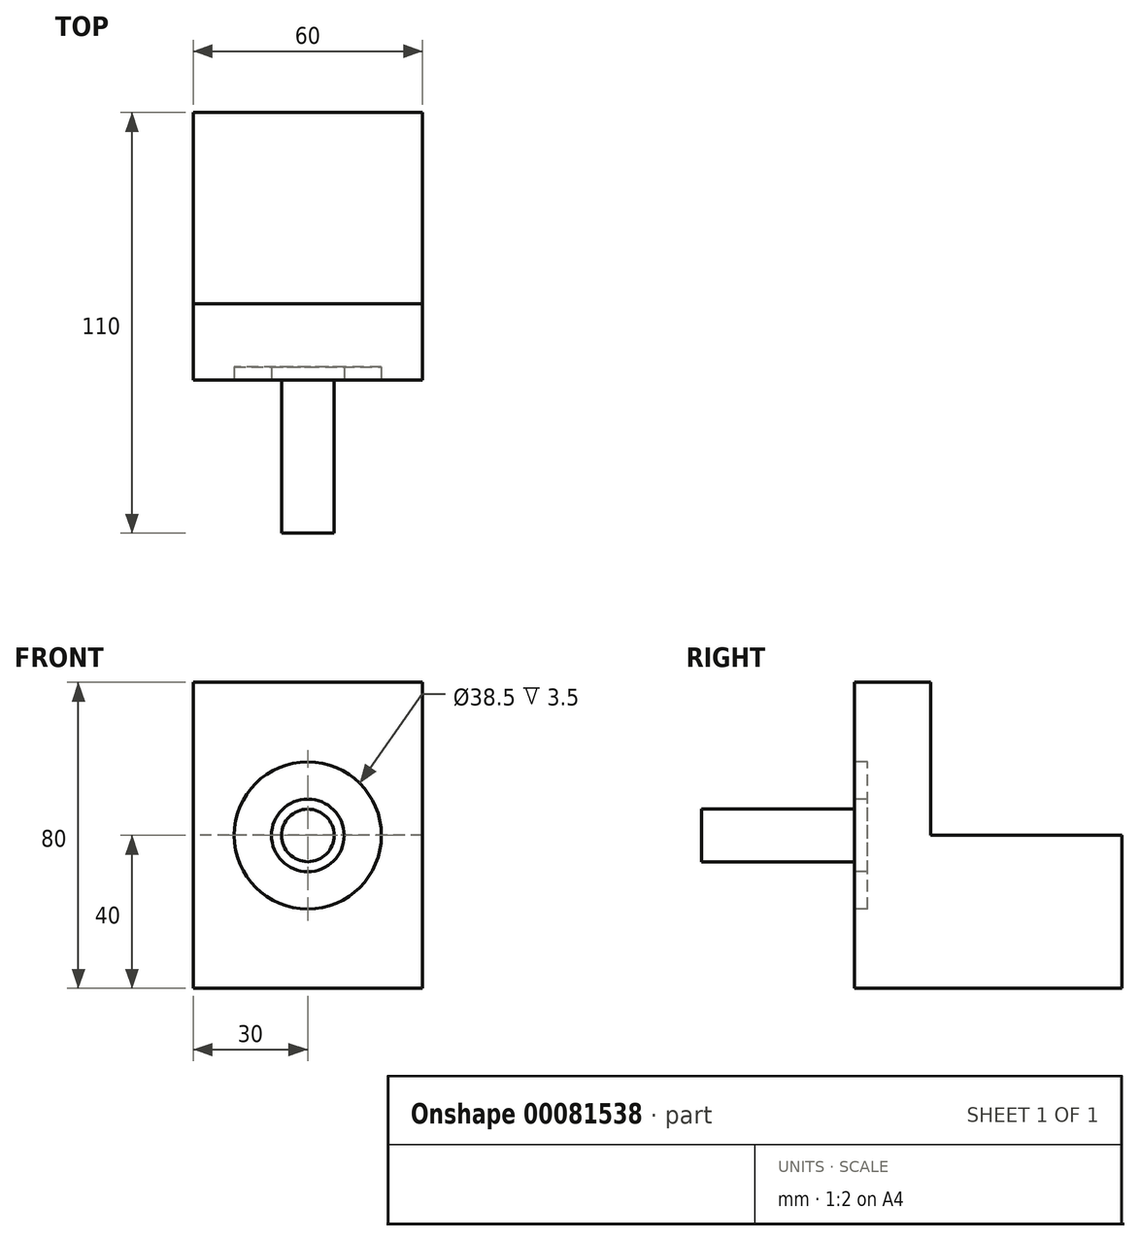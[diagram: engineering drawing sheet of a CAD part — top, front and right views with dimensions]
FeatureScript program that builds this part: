
annotation { "Feature Type Name" : "Feature", "Feature Type Description" : "" }
export const myFeature = defineFeature(function(context is Context, id is Id, definition is map)
    precondition{}
    {
        {
            var Q0;
            Q0=qCreatedBy(makeId("Front.planeOp"),FACE);
            var sketch = newSketch(context, id + "F0", { "sketchPlane" : qUnion([Q0])});
            skLineSegment(sketch, "E0", {"start": v(-30, 0) * mm, "end": v(30, 0) * mm});
            skLineSegment(sketch, "E1", {"start": v(30, 0) * mm, "end": v(30, 80) * mm});
            skLineSegment(sketch, "E2", {"start": v(30, 80) * mm, "end": v(-30, 80) * mm});
            skLineSegment(sketch, "E3", {"start": v(-30, 80) * mm, "end": v(-30, 0) * mm});
            skLineSegment(sketch, "E4", {"start": v(0, 0) * mm, "end": v(0, 40) * mm, "construction": true});
            skCircle(sketch, "E5", {"center": v(0, 40) * mm, "radius": 6.88 * mm});
            skSolve(sketch);
        }
        {
            var Q0;
            Q0=makeQuery(id+"F0.imprint","IMPRINT",FACE,{"disambiguationData":[TD([[makeQuery(id+"F0.imprint","IMPRINT",EDGE,{"derivedFrom":sQuery(id+"F0.wireOp",EDGE,"E5")}),1.0]])]});
            extrude(context, id + "F1", {"entities" : qUnion([Q0]), "depth" : 40 * mm});
        }
        {
            var Q0;
            Q0=makeQuery(id+"F0.imprint","IMPRINT",FACE,{"disambiguationData":[TD([[makeQuery(id+"F0.imprint","IMPRINT",EDGE,{"derivedFrom":sQuery(id+"F0.wireOp",EDGE,"E5")}),1.0]])]});
            var Q1;
            Q1=makeQuery(id+"F0.imprint","IMPRINT",FACE,{"disambiguationData":[TD([[makeQuery(id+"F0.imprint","IMPRINT",EDGE,{"derivedFrom":sQuery(id+"F0.wireOp",EDGE,"E0")}),1.0]])]});
            extrude(context, id + "F2", {"entities" : qUnion([Q0, Q1]), "operationType" : NewBodyOperationType.ADD, "oppositeDirection" : true, "depth" : 20 * mm});
        }
        {
            var Q0;
            Q0=makeQuery(id+"F0.imprint","IMPRINT",FACE,{"disambiguationData":[TD([[makeQuery(id+"F0.imprint","IMPRINT",EDGE,{"derivedFrom":sQuery(id+"F0.wireOp",EDGE,"E0")}),1.0]])]});
            var sketch = newSketch(context, id + "F3", { "sketchPlane" : qUnion([Q0])});
            skCircle(sketch, "E6", {"center": v(0, 40) * mm, "radius": 9.5 * mm});
            skCircle(sketch, "E7", {"center": v(0, 40) * mm, "radius": 19.25 * mm});
            skSolve(sketch);
        }
        {
            var Q0;
            Q0=makeQuery(id+"F3.imprint","IMPRINT",FACE,{"disambiguationData":[TD([[makeQuery(id+"F3.imprint","IMPRINT",EDGE,{"derivedFrom":sQuery(id+"F3.wireOp",EDGE,"E6")}),-1.0]])]});
            extrude(context, id + "F4", {"entities" : qUnion([Q0]), "operationType" : NewBodyOperationType.REMOVE, "oppositeDirection" : true, "depth" : 3.5 * mm});
        }
        {
            var Q0;
            Q0=makeQuery(id+"F2.opExtrude","CAP_FACE",FACE,{"disambiguationData":[OSD([sQuery(id+"F0.wireOp",EDGE,"E0"),sQuery(id+"F0.wireOp",EDGE,"E1"),sQuery(id+"F0.wireOp",EDGE,"E2"),sQuery(id+"F0.wireOp",EDGE,"E3")])],"isStart":false});
            var sketch = newSketch(context, id + "F5", { "sketchPlane" : qUnion([Q0])});
            skLineSegment(sketch, "E8.bottom", {"start": v(-30, 0) * mm, "end": v(30, 0) * mm});
            skLineSegment(sketch, "E8.top", {"start": v(-30, 40) * mm, "end": v(30, 40) * mm});
            skLineSegment(sketch, "E8.left", {"start": v(-30, 0) * mm, "end": v(-30, 40) * mm});
            skLineSegment(sketch, "E8.right", {"start": v(30, 0) * mm, "end": v(30, 40) * mm});
            skSolve(sketch);
        }
        {
            var Q0;
            Q0=makeQuery(id+"F5.imprint","IMPRINT",FACE,{"disambiguationData":[TD([[makeQuery(id+"F5.imprint","IMPRINT",EDGE,{"derivedFrom":sQuery(id+"F5.wireOp",EDGE,"E8.bottom")}),-1.0]])]});
            extrude(context, id + "F6", {"entities" : qUnion([Q0]), "operationType" : NewBodyOperationType.ADD, "depth" : 50 * mm});
        }
    });
